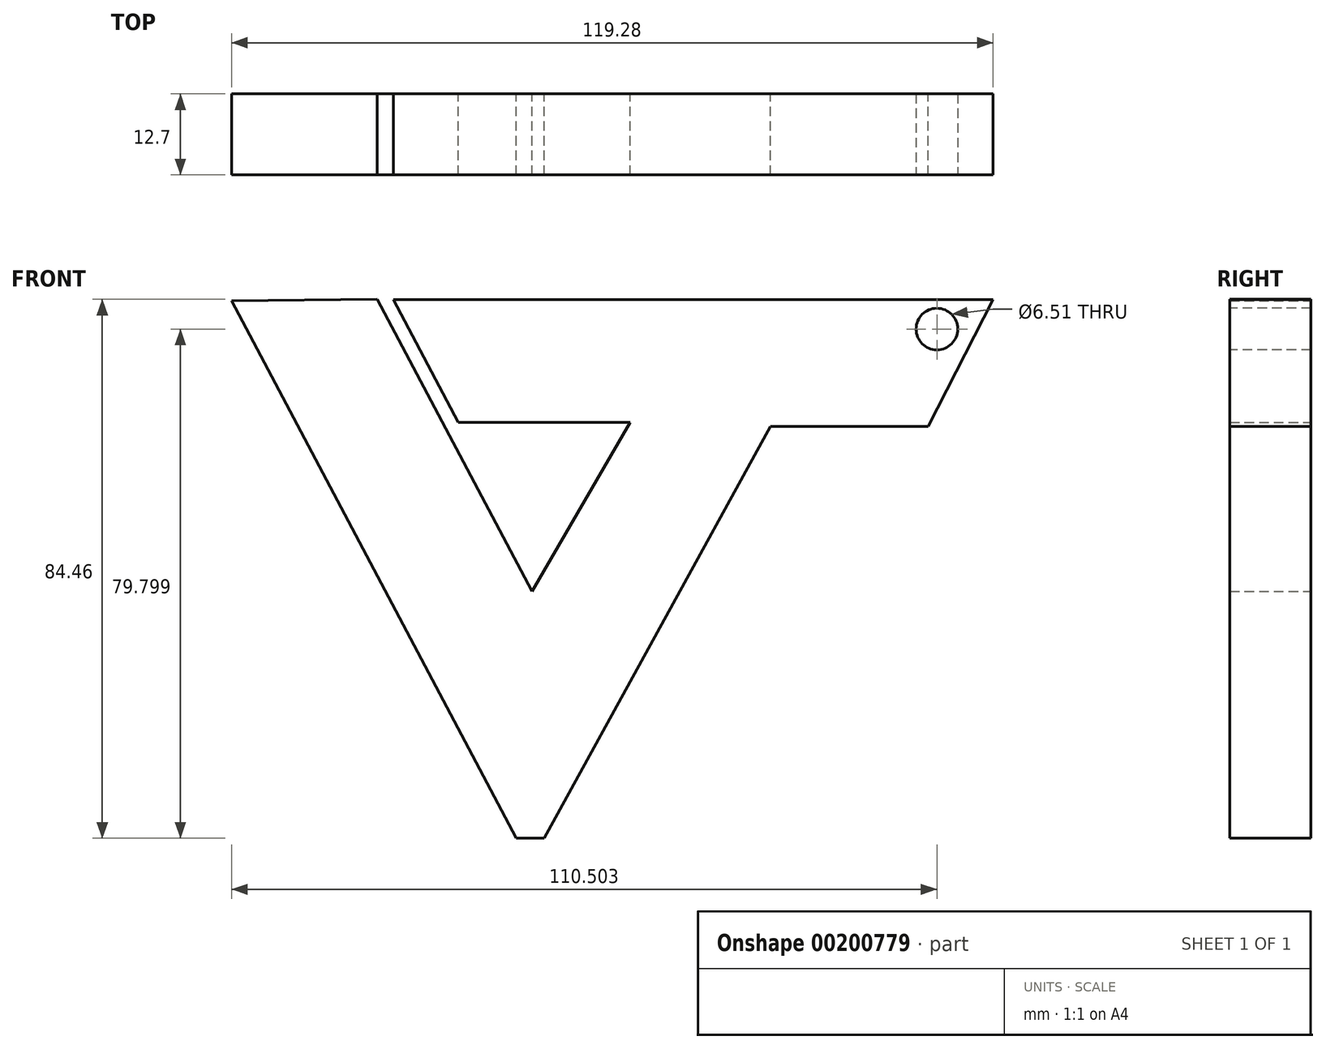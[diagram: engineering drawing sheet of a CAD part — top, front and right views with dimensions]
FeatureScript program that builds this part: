
annotation { "Feature Type Name" : "Feature", "Feature Type Description" : "" }
export const myFeature = defineFeature(function(context is Context, id is Id, definition is map)
    precondition{}
    {
        {
            var Q0;
            Q0=qCreatedBy(makeId("Front.planeOp"),FACE);
            var sketch = newSketch(context, id + "F0", { "sketchPlane" : qUnion([Q0])});
            skLineSegment(sketch, "E0", {"start": v(-49, 55.82) * mm, "end": v(-4.4, -28.39) * mm});
            skLineSegment(sketch, "E1", {"start": v(-4.4, -28.39) * mm, "end": v(0, -28.39) * mm});
            skLineSegment(sketch, "E2", {"start": v(0, -28.39) * mm, "end": v(35.44, 36.12) * mm});
            skLineSegment(sketch, "E3", {"start": v(35.44, 36.12) * mm, "end": v(60.1, 36.12) * mm});
            skLineSegment(sketch, "E4", {"start": v(60.1, 36.12) * mm, "end": v(70.3, 56.04) * mm});
            skLineSegment(sketch, "E5", {"start": v(70.3, 56.04) * mm, "end": v(-23.64, 56.04) * mm});
            skLineSegment(sketch, "E6", {"start": v(-23.64, 56.04) * mm, "end": v(-13.45, 36.8) * mm});
            skLineSegment(sketch, "E7", {"start": v(-13.45, 36.8) * mm, "end": v(13.48, 36.8) * mm});
            skLineSegment(sketch, "E8", {"start": v(13.48, 36.8) * mm, "end": v(-1.91, 10.32) * mm});
            skLineSegment(sketch, "E9", {"start": v(-1.91, 10.32) * mm, "end": v(-26.14, 56.07) * mm});
            skLineSegment(sketch, "E10", {"start": v(-26.14, 56.07) * mm, "end": v(-49, 55.82) * mm});
            skSolve(sketch);
        }
        {
            var Q0;
            Q0 = qSketchRegion(id + "F0", true);
            extrude(context, id + "F1", {"entities" : qUnion([Q0]), "depth" : 12.7 * mm});
        }
        {
            var Q0;
            Q0=makeQuery(id+"F1.opExtrude","CAP_FACE",FACE,{"disambiguationData":[OSD([sQuery(id+"F0.wireOp",EDGE,"E0"),sQuery(id+"F0.wireOp",EDGE,"E1"),sQuery(id+"F0.wireOp",EDGE,"E2"),sQuery(id+"F0.wireOp",EDGE,"E3"),sQuery(id+"F0.wireOp",EDGE,"E4"),sQuery(id+"F0.wireOp",EDGE,"E5"),sQuery(id+"F0.wireOp",EDGE,"E6"),sQuery(id+"F0.wireOp",EDGE,"E7"),sQuery(id+"F0.wireOp",EDGE,"E8"),sQuery(id+"F0.wireOp",EDGE,"E9"),sQuery(id+"F0.wireOp",EDGE,"E10")])],"isStart":false});
            var sketch = newSketch(context, id + "F2", { "sketchPlane" : qUnion([Q0])});
            skCircle(sketch, "E11", {"center": v(61.51, 51.4) * mm, "radius": 3.25 * mm});
            skSolve(sketch);
        }
        {
            var Q0;
            Q0 = qSketchRegion(id + "F2", true);
            extrude(context, id + "F3", {"entities" : qUnion([Q0]), "operationType" : NewBodyOperationType.REMOVE, "endBound" : BoundingType.THROUGH_ALL, "oppositeDirection" : true, "depth" : 25.4 * mm});
        }
    });
